# Revit family: Exhaust_Fan-Commercial-BroanNutone-Losone_ESelect-Inline
name_source: partatom
category: Mechanical Equipment
units: mm (PartAtom-declared; Revit-internal decimal feet)

## family parameters
Cut with Voids When Loaded = No
Host = Face
OmniClass Number = 23.75.35.17.17
OmniClass Title = Room Air Circulation Fans
Part Type = Normal
Room Calculation Point = No
Round Connector Dimension = Use Radius
Shared = No

## types (5) — shared parameters
Assembly Code = E1090900
Cover Finish = Plastic - Broan NuTone - White
Default Elevation = 4' - 0"
Electrical Connector = Electrical Connection
Exhaust Connector = Exhaust Connection
Exhaust Diameter = 0' - 6"
Exhaust Radius = 0' - 3"
Fan Body Finish = Metal - Broan NuTone - Steel
Fan Wattage = 8 W
Frequency = 60 Hz
Height = 6' - 5 5/8"
Housing Height = 0' - 7 5/8"
Housing Length = 0' - 10 1/32"
Housing Width = 0' - 11 3/8"
Length = 1' - 2"
Manufacturer = Broan
Noise = 1.2
Number of Poles = 1
Phase = 1
Power Factor = 1
Product Documentation Link = https://www.broan-nutone.com
Product Name = LOSONE-E SELECT™ , Inline Ventilation Fan, ENERGY STAR®
Product Page URL = https://www.broan-nutone.com
URL = https://www.broan-nutone.com
Voltage = 120 V
Width = 1' - 2"

## per-type parameters (varying)
| type | Description | Model |
| 100 CFM | LOSONE-E SELECT™ , 100CFM Inline Ventilation Fan, ENERGY STAR® | L100EL |
| 150 CFM | LOSONE-E SELECT™ , 150CFM Inline Ventilation Fan, ENERGY STAR® | L150EL |
| 200 CFM | LOSONE-E SELECT™ , 200CFM Inline Ventilation Fan, ENERGY STAR® | L200EL |
| 250 CFM | LOSONE-E SELECT™ , 250CFM Inline Ventilation Fan, ENERGY STAR® | L250EL |
| 300 CFM | LOSONE-E SELECT™ , 300CFM Inline Ventilation Fan, ENERGY STAR® | L300EL |

note: column(s) folded — value = type name in every type: Air Volume

## geometry (parser evidence)
native form markers: Sweep x3
no freeform markers — native parametric forms only
